# Revit family: IS_Eurovit_V4931_BIM_DE
name_source: partatom
category: Plumbing Fixtures
revit_build: Autodesk Revit MEP 2016 (Build: 20161004_0715(x64)
units: mm (PartAtom-declared; Revit-internal decimal feet)

## family parameters
Always vertical = No
Cut with Voids When Loaded = No
OmniClass Number = 23.45.05.14.27
OmniClass Title = Bidets
Part Type = Normal
Room Calculation Point = No
Round Connector Dimension = Use Diameter
Shared = No
Work Plane-Based = No

## types (1)
- V493101 - EUROVIT wall mounted bidet 360x520mm, 1 taphole
    Accessories = www.idealstandard.de\ersatzteile
    AssetType = Fixed
    BIMObjectName = ISI_IdealStandard_Bidets_Eurovit_V493101
    BIMobject category = Bidets
    BOSUseNativeGeometries = 1
    BarCode = 8595095903548
    Brand = Ideal Standard
    Brand url = http://www.idealstandard.de
    CodePerformance = DIN EN 14528 CL 25, DIN EN 35
    Color = White
    ConnectionType = Plumbing
    Cost = 0 $
    CurrencyUnit = €
    CurrentRevision = 1
    Date of publishing = 20/12/2017
    Description = IS Wandbidet EUROVIT, 1 Hl., 360x520x400mm, Weiß
    DrainSize = 0 mm  [stored 0 ft]
    DurationUnit = Year
    EAN code = https://8595095903548
    Edition number = 1
    ExpectedLife = 25
    Features = IS Wandbidet EUROVIT, 1 Hl., 360x520x400mm, Weiß
    Finish = White
    IFC Classification = Sanitary Terminal
    IfcExportAs = IfcSanitaryTerminalType
    Installation instructions = http://www.idealstandard.de
    InstallationInstructions = www.idealstandard.de\produkte
    MainColor = White
    MaintenanceInformation = www.idealstandard.de\produkte
    Manufacturer name = Ideal Standard
    ManufacturerURL = http://www.idealstandard.de
    Material = Vitreous china
    Material main = Ceramics
    Model = V493101
    ModelNumber = V493101
    ModelReference = IS Wandbidet EUROVIT, 1 Hl., 360x520x400mm, Weiß
    NBS Reference Code = 35-06-11
    NBS Reference Description = Bidets
    Name = Bidets_Eurovit_V493101
    NettWeight = 15 Kg
    Nominal height = 350
    Nominal width = 360
    NominalDepth = 519 mm
    NominalHeight = 375 mm
    NominalLength = 519 mm
    NominalWidth = 360 mm  [stored 1.1811 ft]
    OmniClass Code = 23-31 23 00
    OmniClass Description = Bidets
    Product Guid = 66c1e63b-a97a-45d6-b192-4ef8f82614a9
    Product SKU = V4931
    Product data url = https://bimobject.com
    Product family = Sanitary
    Product group = Bidet
    Product name = EUROVIT wall mounted bidet 360x520mm, 1 taphole
    Product url = http://www.idealstandard.de
    ProductInformation = www.idealstandard.de/produkte
    QR code = http://bimobject.com
    Shape = Sculptured
    Size = 375 x 519 x 360mm
    Space = Internal
    SpareParts = www.idealstandard.de/ersatzteile
    Technical description = http://www.idealstandard.de
    URL = http://www.idealstandard.de
    Uniclass 2.0 Code = PR-35-06-11
    Uniclass 2.0 Description = Bidets
    Uniclass 2015 Code = Pr_40_20_06_11
    Uniclass 2015 Name = Bidets
    Uniclass2015Code = Pr_40_20_06_11
    Uniclass2015Title = Bidets
    Uniclass2015Version = Products v1.1
    Version = 1
    VolumeUnits = Litres
    Weight Net (Kg) = 15

note: [stored X ft] marks values corroborated as IEEE doubles in the binary element streams (Revit-internal decimal feet)

## geometry (parser evidence)
native form markers: Blend x4
no freeform markers — native parametric forms only
